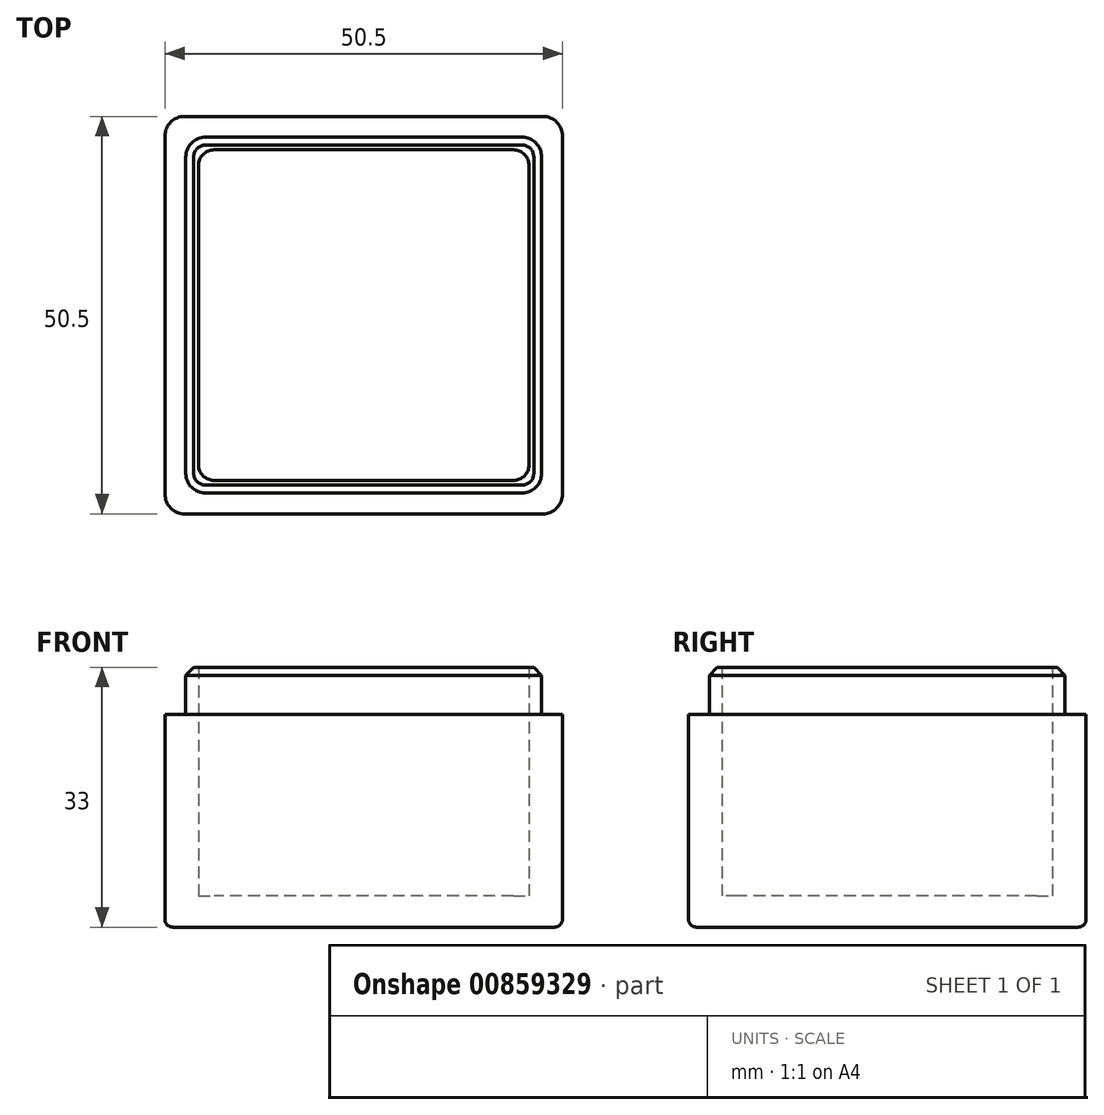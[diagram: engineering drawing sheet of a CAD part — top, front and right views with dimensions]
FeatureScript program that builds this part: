
annotation { "Feature Type Name" : "Feature", "Feature Type Description" : "" }
export const myFeature = defineFeature(function(context is Context, id is Id, definition is map)
    precondition{}
    {
        {
            var Q0;
            Q0=qCreatedBy(makeId("Top.planeOp"),FACE);
            var sketch = newSketch(context, id + "F0", { "sketchPlane" : qUnion([Q0])});
            skLineSegment(sketch, "E0.bottom", {"start": v(25.25, 25.25) * mm, "end": v(-25.25, 25.25) * mm});
            skLineSegment(sketch, "E0.top", {"start": v(25.25, -25.25) * mm, "end": v(-25.25, -25.25) * mm});
            skLineSegment(sketch, "E0.left", {"start": v(25.25, 25.25) * mm, "end": v(25.25, -25.25) * mm});
            skLineSegment(sketch, "E0.right", {"start": v(-25.25, 25.25) * mm, "end": v(-25.25, -25.25) * mm});
            skPoint(sketch, "E0.middle", {"position": v(0, 0) * mm});
            skSolve(sketch);
        }
        {
            var Q0;
            Q0=qSketchRegion(id+"F0",true);
            extrude(context, id + "F1", {"entities" : qUnion([Q0]), "depth" : (2 + 19.3 + 1.7 + 4) * mm, "offsetDistance" : 25 * mm});
        }
        {
            var Q0;
            Q0=makeQuery(id+"F1.opExtrude","CAP_FACE",FACE,{"disambiguationData":[OSD([sQuery(id+"F0.wireOp",EDGE,"E0.bottom"),sQuery(id+"F0.wireOp",EDGE,"E0.top"),sQuery(id+"F0.wireOp",EDGE,"E0.left"),sQuery(id+"F0.wireOp",EDGE,"E0.right")])],"isStart":false});
            var sketch = newSketch(context, id + "F2", { "sketchPlane" : qUnion([Q0])});
            skLineSegment(sketch, "E1.bottom", {"start": v(22.6, 22.6) * mm, "end": v(-22.6, 22.6) * mm});
            skLineSegment(sketch, "E1.top", {"start": v(22.6, -22.6) * mm, "end": v(-22.6, -22.6) * mm});
            skLineSegment(sketch, "E1.left", {"start": v(22.6, 22.6) * mm, "end": v(22.6, -22.6) * mm});
            skLineSegment(sketch, "E1.right", {"start": v(-22.6, 22.6) * mm, "end": v(-22.6, -22.6) * mm});
            skPoint(sketch, "E1.middle", {"position": v(0, 0) * mm});
            skSolve(sketch);
        }
        {
            var Q0;
            Q0=qSketchRegion(id+"F2",true);
            extrude(context, id + "F3", {"entities" : qUnion([Q0]), "operationType" : NewBodyOperationType.ADD, "depth" : 6 * mm, "offsetDistance" : 25 * mm});
        }
        {
            var Q0;
            Q0=makeQuery(id+"F1.opExtrude","CAP_FACE",FACE,{"disambiguationData":[OSD([sQuery(id+"F0.wireOp",EDGE,"E0.bottom"),sQuery(id+"F0.wireOp",EDGE,"E0.top"),sQuery(id+"F0.wireOp",EDGE,"E0.left"),sQuery(id+"F0.wireOp",EDGE,"E0.right")])],"isStart":false});
            var sketch = newSketch(context, id + "F4", { "sketchPlane" : qUnion([Q0])});
            skLineSegment(sketch, "E2.bottom", {"start": v(21, 21) * mm, "end": v(-21, 21) * mm});
            skLineSegment(sketch, "E2.top", {"start": v(21, -21) * mm, "end": v(-21, -21) * mm});
            skLineSegment(sketch, "E2.left", {"start": v(21, 21) * mm, "end": v(21, -21) * mm});
            skLineSegment(sketch, "E2.right", {"start": v(-21, 21) * mm, "end": v(-21, -21) * mm});
            skPoint(sketch, "E2.middle", {"position": v(0, 0) * mm});
            skSolve(sketch);
        }
        {
            var Q0;
            Q0=qSketchRegion(id+"F4",true);
            extrude(context, id + "F5", {"entities" : qUnion([Q0]), "operationType" : NewBodyOperationType.REMOVE, "endBound" : BoundingType.UP_TO_NEXT, "depth" : 25 * mm, "offsetDistance" : 25 * mm, "hasSecondDirection" : true, "secondDirectionOppositeDirection" : true, "secondDirectionDepth" : 23 * mm});
        }
        {
            var Q0;
            Q0=makeQuery(id+"F1.opExtrude","SWEPT_EDGE",EDGE,{"disambiguationData":[OSD([sQuery(id+"F0.wireOp",EDGE,"E0.bottom"),sQuery(id+"F0.wireOp",EDGE,"E0.right")])]});
            var Q1;
            Q1=makeQuery(id+"F1.opExtrude","SWEPT_EDGE",EDGE,{"disambiguationData":[OSD([sQuery(id+"F0.wireOp",EDGE,"E0.top"),sQuery(id+"F0.wireOp",EDGE,"E0.right")])]});
            var Q2;
            Q2=makeQuery(id+"F1.opExtrude","SWEPT_EDGE",EDGE,{"disambiguationData":[OSD([sQuery(id+"F0.wireOp",EDGE,"E0.top"),sQuery(id+"F0.wireOp",EDGE,"E0.left")])]});
            var Q3;
            Q3=makeQuery(id+"F1.opExtrude","SWEPT_EDGE",EDGE,{"disambiguationData":[OSD([sQuery(id+"F0.wireOp",EDGE,"E0.bottom"),sQuery(id+"F0.wireOp",EDGE,"E0.left")])]});
            var Q4;
            Q4=makeQuery(id+"F3.opExtrude","SWEPT_EDGE",EDGE,{"disambiguationData":[OSD([sQuery(id+"F2.wireOp",EDGE,"E1.bottom"),sQuery(id+"F2.wireOp",EDGE,"E1.right")])]});
            var Q5;
            Q5=makeQuery(id+"F3.opExtrude","SWEPT_EDGE",EDGE,{"disambiguationData":[OSD([sQuery(id+"F2.wireOp",EDGE,"E1.top"),sQuery(id+"F2.wireOp",EDGE,"E1.right")])]});
            var Q6;
            Q6=makeQuery(id+"F3.opExtrude","SWEPT_EDGE",EDGE,{"disambiguationData":[OSD([sQuery(id+"F2.wireOp",EDGE,"E1.top"),sQuery(id+"F2.wireOp",EDGE,"E1.left")])]});
            var Q7;
            Q7=makeQuery(id+"F3.opExtrude","SWEPT_EDGE",EDGE,{"disambiguationData":[OSD([sQuery(id+"F2.wireOp",EDGE,"E1.bottom"),sQuery(id+"F2.wireOp",EDGE,"E1.left")])]});
            fillet(context, id + "F6", {"entities" : qUnion([Q0, Q1, Q2, Q3, Q4, Q5, Q6, Q7]), "radius" : 2.5 * mm, "tangentPropagation" : true, "allowEdgeOverflow" : false});
        }
        {
            var Q0;
            Q0=makeQuery(id+"F5.boolean.opBoolean","COPY",EDGE,{"derivedFrom":makeQuery(id+"F5.opExtrude","SWEPT_EDGE",EDGE,{"disambiguationData":[OSD([sQuery(id+"F4.wireOp",EDGE,"E2.bottom"),sQuery(id+"F4.wireOp",EDGE,"E2.right")])]})});
            var Q1;
            Q1=makeQuery(id+"F5.boolean.opBoolean","COPY",EDGE,{"derivedFrom":makeQuery(id+"F5.opExtrude","SWEPT_EDGE",EDGE,{"disambiguationData":[OSD([sQuery(id+"F4.wireOp",EDGE,"E2.bottom"),sQuery(id+"F4.wireOp",EDGE,"E2.left")])]})});
            var Q2;
            Q2=makeQuery(id+"F5.boolean.opBoolean","COPY",EDGE,{"derivedFrom":makeQuery(id+"F5.opExtrude","SWEPT_EDGE",EDGE,{"disambiguationData":[OSD([sQuery(id+"F4.wireOp",EDGE,"E2.top"),sQuery(id+"F4.wireOp",EDGE,"E2.left")])]})});
            var Q3;
            Q3=makeQuery(id+"F5.boolean.opBoolean","COPY",EDGE,{"derivedFrom":makeQuery(id+"F5.opExtrude","SWEPT_EDGE",EDGE,{"disambiguationData":[OSD([sQuery(id+"F4.wireOp",EDGE,"E2.top"),sQuery(id+"F4.wireOp",EDGE,"E2.right")])]})});
            fillet(context, id + "F7", {"entities" : qUnion([Q0, Q1, Q2, Q3]), "radius" : 2 * mm, "tangentPropagation" : true, "allowEdgeOverflow" : false});
        }
        {
            var Q0;
            Q0=makeQuery(id+"F3.opExtrude","CAP_EDGE",EDGE,{"disambiguationData":[OSD([sQuery(id+"F2.wireOp",EDGE,"E1.right")])],"isStart":false});
            chamfer(context, id + "F8", {"entities" : qUnion([Q0]), "width" : 1 * mm, "tangentPropagation" : true});
        }
        {
            var Q0;
            Q0=makeQuery(id+"F1.opExtrude","CAP_EDGE",EDGE,{"disambiguationData":[OSD([sQuery(id+"F0.wireOp",EDGE,"E0.bottom")])],"isStart":true});
            fillet(context, id + "F9", {"entities" : qUnion([Q0]), "radius" : 1 * mm, "tangentPropagation" : true, "allowEdgeOverflow" : false});
        }
    });
